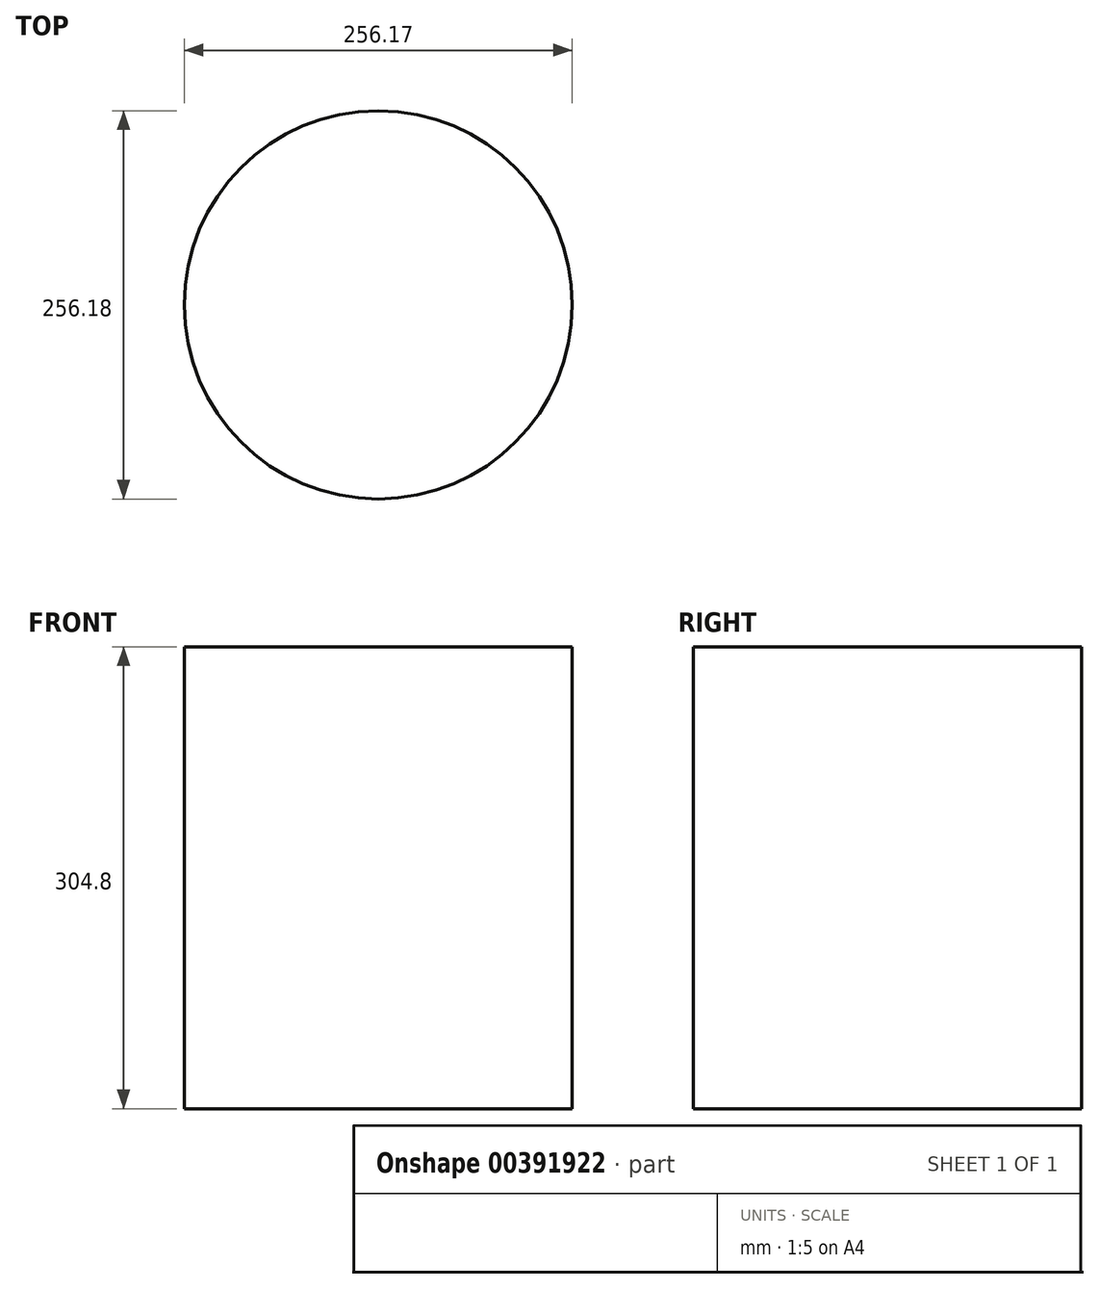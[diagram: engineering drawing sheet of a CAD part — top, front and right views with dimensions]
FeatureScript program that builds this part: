
annotation { "Feature Type Name" : "Feature", "Feature Type Description" : "" }
export const myFeature = defineFeature(function(context is Context, id is Id, definition is map)
    precondition{}
    {
        {
            var Q0;
            Q0=qCreatedBy(makeId("Top.planeOp"),FACE);
            var sketch = newSketch(context, id + "F0", { "sketchPlane" : qUnion([Q0])});
            skCircle(sketch, "E0", {"center": v(-32.43, -36.62) * mm, "radius": 128.09 * mm});
            skSolve(sketch);
        }
        {
            var Q0;
            Q0 = qSketchRegion(id + "F0", true);
            var Q1;
            Q1=sQuery(id+"F0.wireOp",EDGE,"E0");
            extrude(context, id + "F1", {"entities" : qUnion([Q0]), "bodyType" : ToolBodyType.SURFACE, "surfaceEntities" : qUnion([Q1]), "depth" : 304.8 * mm});
        }
    });
